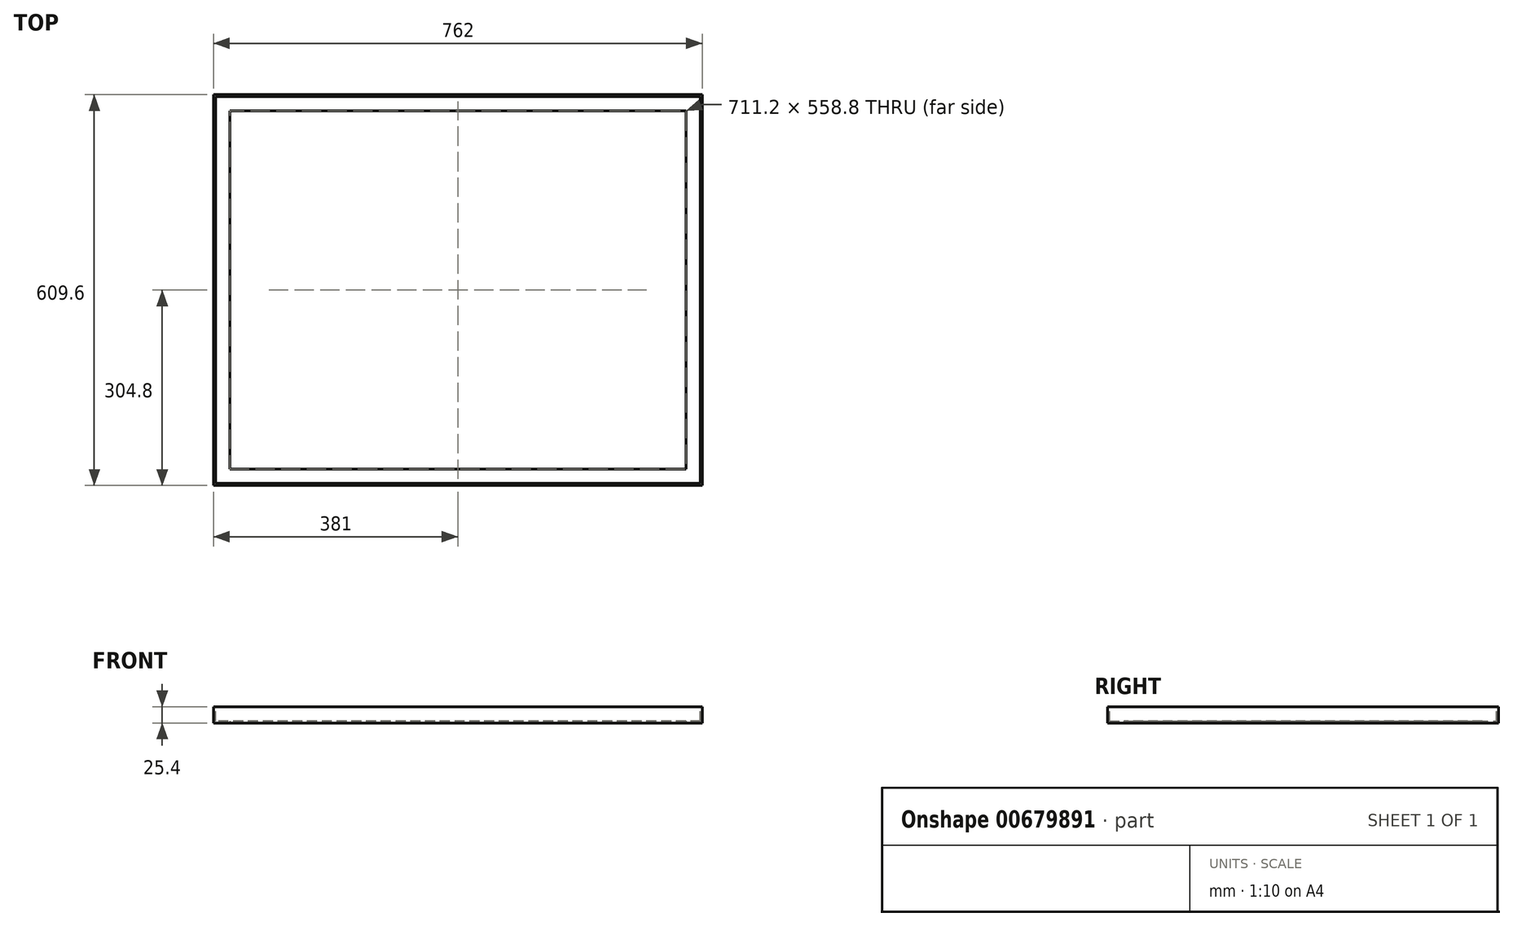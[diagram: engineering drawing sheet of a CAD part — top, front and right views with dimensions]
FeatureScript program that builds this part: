
annotation { "Feature Type Name" : "Feature", "Feature Type Description" : "" }
export const myFeature = defineFeature(function(context is Context, id is Id, definition is map)
    precondition{}
    {
        {
            var Q0;
            Q0=qCreatedBy(makeId("Top.planeOp"),FACE);
            var sketch = newSketch(context, id + "F0", { "sketchPlane" : qUnion([Q0])});
            skLineSegment(sketch, "E0.bottom", {"start": v(0, 0) * mm, "end": v(762, 0) * mm});
            skLineSegment(sketch, "E0.top", {"start": v(0, 609.6) * mm, "end": v(762, 609.6) * mm});
            skLineSegment(sketch, "E0.left", {"start": v(0, 0) * mm, "end": v(0, 609.6) * mm});
            skLineSegment(sketch, "E0.right", {"start": v(762, 0) * mm, "end": v(762, 609.6) * mm});
            skSolve(sketch);
        }
        {
            var Q0;
            Q0 = qSketchRegion(id + "F0", true);
            extrude(context, id + "F1", {"entities" : qUnion([Q0]), "depth" : 25.4 * mm, "offsetDistance" : 25.4 * mm});
        }
        {
            var Q0;
            Q0=makeQuery(id+"F1.opExtrude","CAP_FACE",FACE,{"disambiguationData":[OSD([sQuery(id+"F0.wireOp",EDGE,"E0.bottom"),sQuery(id+"F0.wireOp",EDGE,"E0.top"),sQuery(id+"F0.wireOp",EDGE,"E0.left"),sQuery(id+"F0.wireOp",EDGE,"E0.right")])],"isStart":false});
            var sketch = newSketch(context, id + "F2", { "sketchPlane" : qUnion([Q0])});
            skLineSegment(sketch, "E1.0", {"start": v(758.83, 606.43) * mm, "end": v(3.18, 606.43) * mm});
            skLineSegment(sketch, "E1.1", {"start": v(758.83, 3.18) * mm, "end": v(758.83, 606.43) * mm});
            skLineSegment(sketch, "E1.2", {"start": v(3.18, 3.18) * mm, "end": v(758.83, 3.18) * mm});
            skLineSegment(sketch, "E1.3", {"start": v(3.18, 606.43) * mm, "end": v(3.18, 3.18) * mm});
            skSolve(sketch);
        }
        {
            var Q0;
            Q0 = qSketchRegion(id + "F2", true);
            extrude(context, id + "F3", {"entities" : qUnion([Q0]), "operationType" : NewBodyOperationType.REMOVE, "oppositeDirection" : true, "depth" : 22.22 * mm, "offsetDistance" : 25.4 * mm});
        }
        {
            var Q0;
            Q0=makeQuery(id+"F1.opExtrude","CAP_FACE",FACE,{"disambiguationData":[OSD([sQuery(id+"F0.wireOp",EDGE,"E0.bottom"),sQuery(id+"F0.wireOp",EDGE,"E0.top"),sQuery(id+"F0.wireOp",EDGE,"E0.left"),sQuery(id+"F0.wireOp",EDGE,"E0.right")])],"isStart":true});
            var sketch = newSketch(context, id + "F4", { "sketchPlane" : qUnion([Q0])});
            skLineSegment(sketch, "E2.0", {"start": v(25.4, -584.2) * mm, "end": v(736.6, -584.2) * mm});
            skLineSegment(sketch, "E2.1", {"start": v(25.4, -25.4) * mm, "end": v(25.4, -584.2) * mm});
            skLineSegment(sketch, "E2.2", {"start": v(736.6, -25.4) * mm, "end": v(25.4, -25.4) * mm});
            skLineSegment(sketch, "E2.3", {"start": v(736.6, -584.2) * mm, "end": v(736.6, -25.4) * mm});
            skSolve(sketch);
        }
        {
            var Q0;
            Q0 = qSketchRegion(id + "F4", true);
            extrude(context, id + "F5", {"entities" : qUnion([Q0]), "operationType" : NewBodyOperationType.REMOVE, "oppositeDirection" : true, "depth" : 25.4 * mm, "offsetDistance" : 25.4 * mm});
        }
    });
